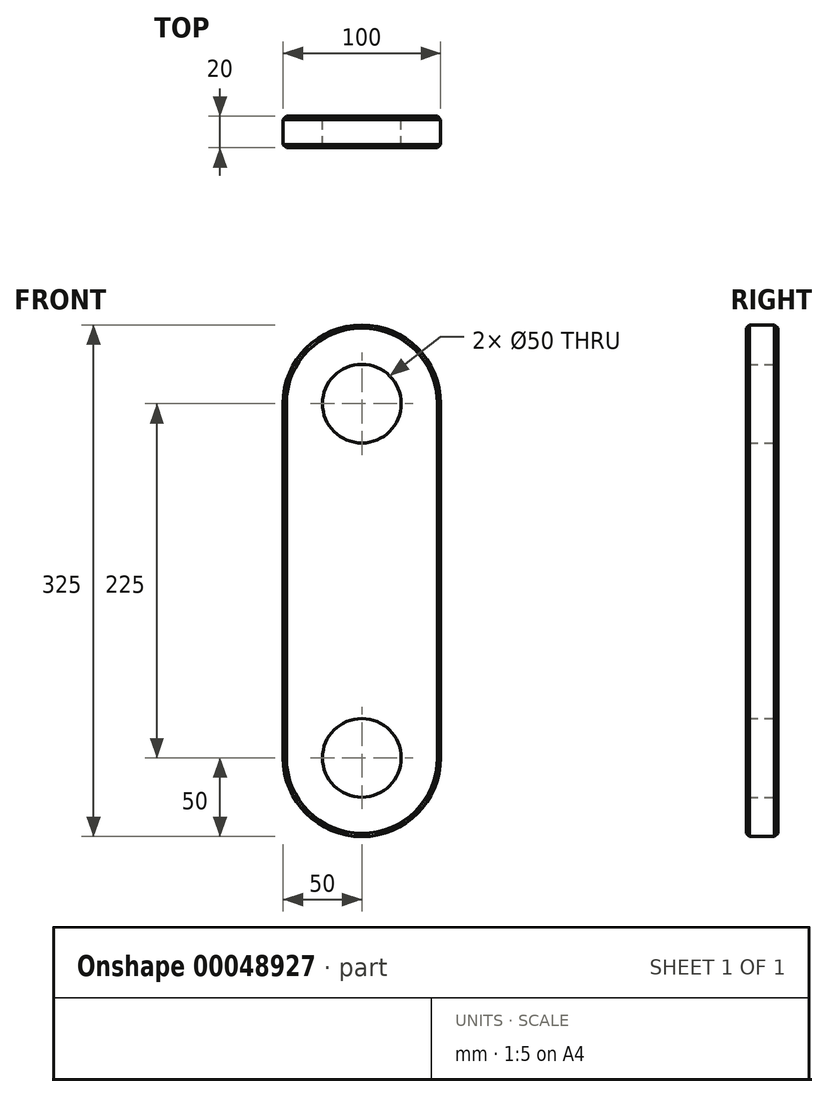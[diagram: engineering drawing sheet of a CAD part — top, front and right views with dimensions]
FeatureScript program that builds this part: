
annotation { "Feature Type Name" : "Feature", "Feature Type Description" : "" }
export const myFeature = defineFeature(function(context is Context, id is Id, definition is map)
    precondition{}
    {
        {
            var Q0;
            Q0=qCreatedBy(makeId("Front.planeOp"),FACE);
            var sketch = newSketch(context, id + "F0", { "sketchPlane" : qUnion([Q0])});
            skLineSegment(sketch, "E0.rect.bottom", {"start": v(-50, 112.5) * mm, "end": v(50, 112.5) * mm, "construction": true});
            skLineSegment(sketch, "E0.rect.top", {"start": v(-50, -112.5) * mm, "end": v(50, -112.5) * mm, "construction": true});
            skLineSegment(sketch, "E0.rect.left", {"start": v(-50, 112.5) * mm, "end": v(-50, -112.5) * mm});
            skLineSegment(sketch, "E0.rect.right", {"start": v(50, 112.5) * mm, "end": v(50, -112.5) * mm});
            skPoint(sketch, "E0.rect.middle", {"position": v(0, 0) * mm});
            skArc(sketch, "E1", {"start": v(-50, 112.5) * mm, "mid": v(0, 162.5) * mm, "end": v(50, 112.5) * mm});
            skArc(sketch, "E2", {"start": v(50, -112.5) * mm, "mid": v(0, -162.5) * mm, "end": v(-50, -112.5) * mm});
            skCircle(sketch, "E3", {"center": v(0, 112.5) * mm, "radius": 25 * mm});
            skCircle(sketch, "E4", {"center": v(0, -112.5) * mm, "radius": 25 * mm});
            skSolve(sketch);
        }
        {
            var Q0;
            Q0=makeQuery(id+"F0.imprint","IMPRINT",FACE,{"disambiguationData":[TD([[makeQuery(id+"F0.imprint","IMPRINT",EDGE,{"derivedFrom":sQuery(id+"F0.wireOp",EDGE,"E0.rect.left")}),1.0]])]});
            extrude(context, id + "F1", {"entities" : qUnion([Q0]), "depth" : 20 * mm});
        }
        {
            var Q0;
            Q0=makeQuery(id+"F1.opExtrude","CAP_EDGE",EDGE,{"disambiguationData":[OSD([sQuery(id+"F0.wireOp",EDGE,"E0.rect.left")])],"isStart":false});
            var Q1;
            Q1=makeQuery(id+"F1.opExtrude","CAP_EDGE",EDGE,{"disambiguationData":[OSD([sQuery(id+"F0.wireOp",EDGE,"E0.rect.right")])],"isStart":true});
            chamfer(context, id + "F2", {"entities" : qUnion([Q0, Q1]), "chamferType" : ChamferType.OFFSET_ANGLE, "width" : 2 * mm, "oppositeDirection" : false, "angle" : 45 * degree, "tangentPropagation" : true});
        }
    });
